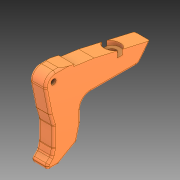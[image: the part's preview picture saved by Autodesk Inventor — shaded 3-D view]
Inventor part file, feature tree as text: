
AUTODESK INVENTOR PART (.ipt)
format: ipt  version: 2020 (Build 240168000, 168)  size: 301,568 bytes
history: native  units: in
note: dims shown in document units (in); Inventor stores cm internally (conversion verified against a paired STEP export)
features: sketch x6, extrude x5, revolve x1, imported_body x1
ambient origin geometry x8: Origin, YZ Plane, XZ Plane, XY Plane, X Axis, Y Axis, Z Axis, Center Point
bodies: Solid1 (feature_tree)
feature tree (13):
  extrude  "Extrusion1"  Depth=0.3937in TaperAngle=0.0deg
  extrude  "Extrusion2"  Depth=0.5906in
  extrude  "Extrusion3"  TaperAngle=90.0deg  [1 undecoded]
  revolve  "Revolution1"  [1 undecoded]
  extrude  "Extrusion4"  TaperAngle=0.0deg  [1 undecoded]
  extrude  "Extrusion5"  Depth=0.3937in
  sketch  "Sketch1"  dims[d0=0.0in d1=0.0in d2=0.3937in d3=0.0in]
  sketch  "Sketch2"  dims[d4=0.1969in d5=0.5906in]
  sketch  "Sketch3"  dims[d6=0.0787in d7=90.0deg]
  sketch  "Sketch4"  dims[d8=0.1575in d9=0.315in]
  sketch  "Sketch5"  dims[d10=0.0787in d11=0.0in d12=0.0in d13=0.0in]
  sketch  "Sketch6"  dims[d14=0.0344in d15=0.3937in d16=0.3937in d17=0.0in d18=0.0in]
  imported_body  "Base1"
note: 3 required parameter values undecoded (feature->parameter linkage not recoverable at this tier; creation-order binding heuristic only, values carry confidence <= 0.55)